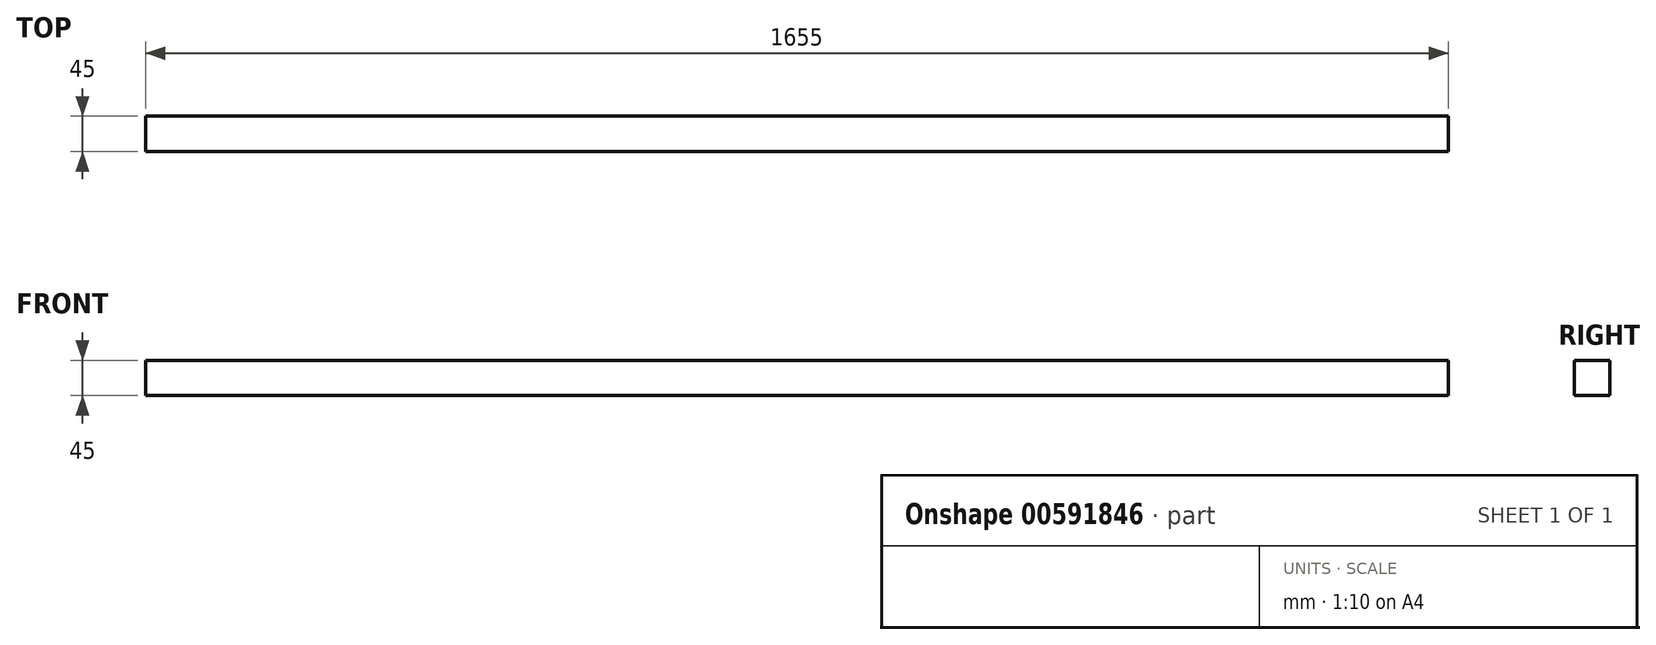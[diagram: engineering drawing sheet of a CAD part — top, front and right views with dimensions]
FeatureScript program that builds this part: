
annotation { "Feature Type Name" : "Feature", "Feature Type Description" : "" }
export const myFeature = defineFeature(function(context is Context, id is Id, definition is map)
    precondition{}
    {
        {
            var Q0;
            Q0=qCreatedBy(makeId("Right.planeOp"),FACE);
            var sketch = newSketch(context, id + "F0", { "sketchPlane" : qUnion([Q0])});
            skLineSegment(sketch, "E0.bottom", {"start": v(0, 0) * mm, "end": v(45, 0) * mm});
            skLineSegment(sketch, "E0.top", {"start": v(0, 45) * mm, "end": v(45, 45) * mm});
            skLineSegment(sketch, "E0.left", {"start": v(0, 0) * mm, "end": v(0, 45) * mm});
            skLineSegment(sketch, "E0.right", {"start": v(45, 0) * mm, "end": v(45, 45) * mm});
            skSolve(sketch);
        }
        {
            var Q0;
            Q0=makeQuery(id+"F0.imprint","IMPRINT",FACE,{"disambiguationData":[TD([[makeQuery(id+"F0.imprint","IMPRINT",EDGE,{"derivedFrom":sQuery(id+"F0.wireOp",EDGE,"E0.bottom")}),1.0]])]});
            extrude(context, id + "F1", {"entities" : qUnion([Q0]), "depth" : 1655 * mm, "offsetDistance" : 25 * mm});
        }
    });
